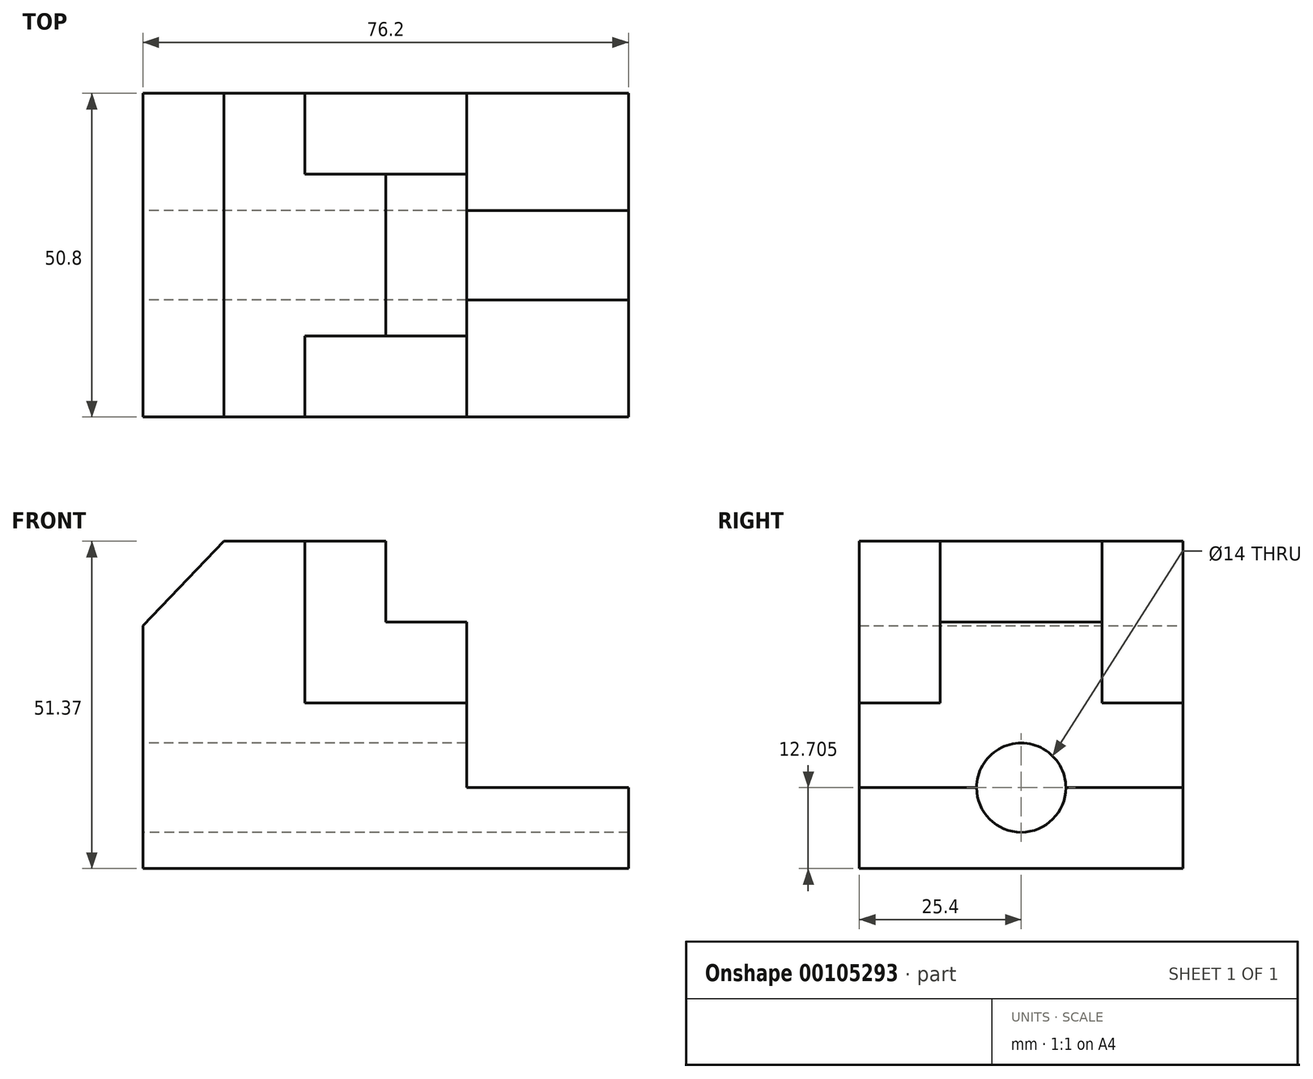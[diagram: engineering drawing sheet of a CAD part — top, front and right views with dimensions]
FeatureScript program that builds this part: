
annotation { "Feature Type Name" : "Feature", "Feature Type Description" : "" }
export const myFeature = defineFeature(function(context is Context, id is Id, definition is map)
    precondition{}
    {
        {
            var Q0;
            Q0=qCreatedBy(makeId("Front.planeOp"),FACE);
            var sketch = newSketch(context, id + "F0", { "sketchPlane" : qUnion([Q0])});
            skLineSegment(sketch, "E0", {"start": v(0, 0) * mm, "end": v(0, 38.1) * mm});
            skLineSegment(sketch, "E1", {"start": v(0, 0) * mm, "end": v(76.2, 0) * mm});
            skLineSegment(sketch, "E2", {"start": v(76.2, 0) * mm, "end": v(76.2, 12.7) * mm});
            skLineSegment(sketch, "E3", {"start": v(76.2, 12.7) * mm, "end": v(50.8, 12.7) * mm});
            skLineSegment(sketch, "E4", {"start": v(50.8, 12.7) * mm, "end": v(50.8, 25.97) * mm});
            skLineSegment(sketch, "E5", {"start": v(50.8, 25.97) * mm, "end": v(25.4, 25.97) * mm});
            skLineSegment(sketch, "E6", {"start": v(25.4, 25.97) * mm, "end": v(25.4, 51.37) * mm});
            skLineSegment(sketch, "E7", {"start": v(25.4, 51.37) * mm, "end": v(12.7, 51.37) * mm});
            skLineSegment(sketch, "E8", {"start": v(12.7, 51.37) * mm, "end": v(0, 38.1) * mm});
            skLineSegment(sketch, "E9", {"start": v(25.4, 51.37) * mm, "end": v(38.1, 51.37) * mm});
            skLineSegment(sketch, "E10", {"start": v(38.1, 51.37) * mm, "end": v(38.1, 38.67) * mm});
            skLineSegment(sketch, "E11", {"start": v(38.1, 38.67) * mm, "end": v(50.8, 38.67) * mm});
            skLineSegment(sketch, "E12", {"start": v(50.8, 38.67) * mm, "end": v(50.8, 25.97) * mm});
            skSolve(sketch);
        }
        {
            var Q0;
            Q0=makeQuery(id+"F0.imprint","IMPRINT",FACE,{"disambiguationData":[TD([[makeQuery(id+"F0.imprint","IMPRINT",EDGE,{"derivedFrom":sQuery(id+"F0.wireOp",EDGE,"E0")}),-1.0]])]});
            extrude(context, id + "F1", {"entities" : qUnion([Q0]), "endBound" : BoundingType.SYMMETRIC, "depth" : 50.8 * mm});
        }
        {
            var Q0;
            Q0=makeQuery(id+"F0.imprint","IMPRINT",FACE,{"disambiguationData":[TD([[makeQuery(id+"F0.imprint","IMPRINT",EDGE,{"derivedFrom":sQuery(id+"F0.wireOp",EDGE,"E5")}),-1.0]])]});
            extrude(context, id + "F2", {"entities" : qUnion([Q0]), "operationType" : NewBodyOperationType.ADD, "endBound" : BoundingType.SYMMETRIC, "depth" : 25.4 * mm});
        }
        {
            var Q0;
            Q0=qCreatedBy(makeId("Right.planeOp"),FACE);
            var sketch = newSketch(context, id + "F3", { "sketchPlane" : qUnion([Q0])});
            skCircle(sketch, "E13", {"center": v(0, 12.7) * mm, "radius": 7 * mm});
            skSolve(sketch);
        }
        {
            var Q0;
            Q0=makeQuery(id+"F3.imprint","IMPRINT",FACE,{"disambiguationData":[TD([[makeQuery(id+"F3.imprint","IMPRINT",EDGE,{"derivedFrom":sQuery(id+"F3.wireOp",EDGE,"E13")}),1.0]])]});
            extrude(context, id + "F4", {"entities" : qUnion([Q0]), "operationType" : NewBodyOperationType.REMOVE, "depth" : 76.2 * mm});
        }
    });
